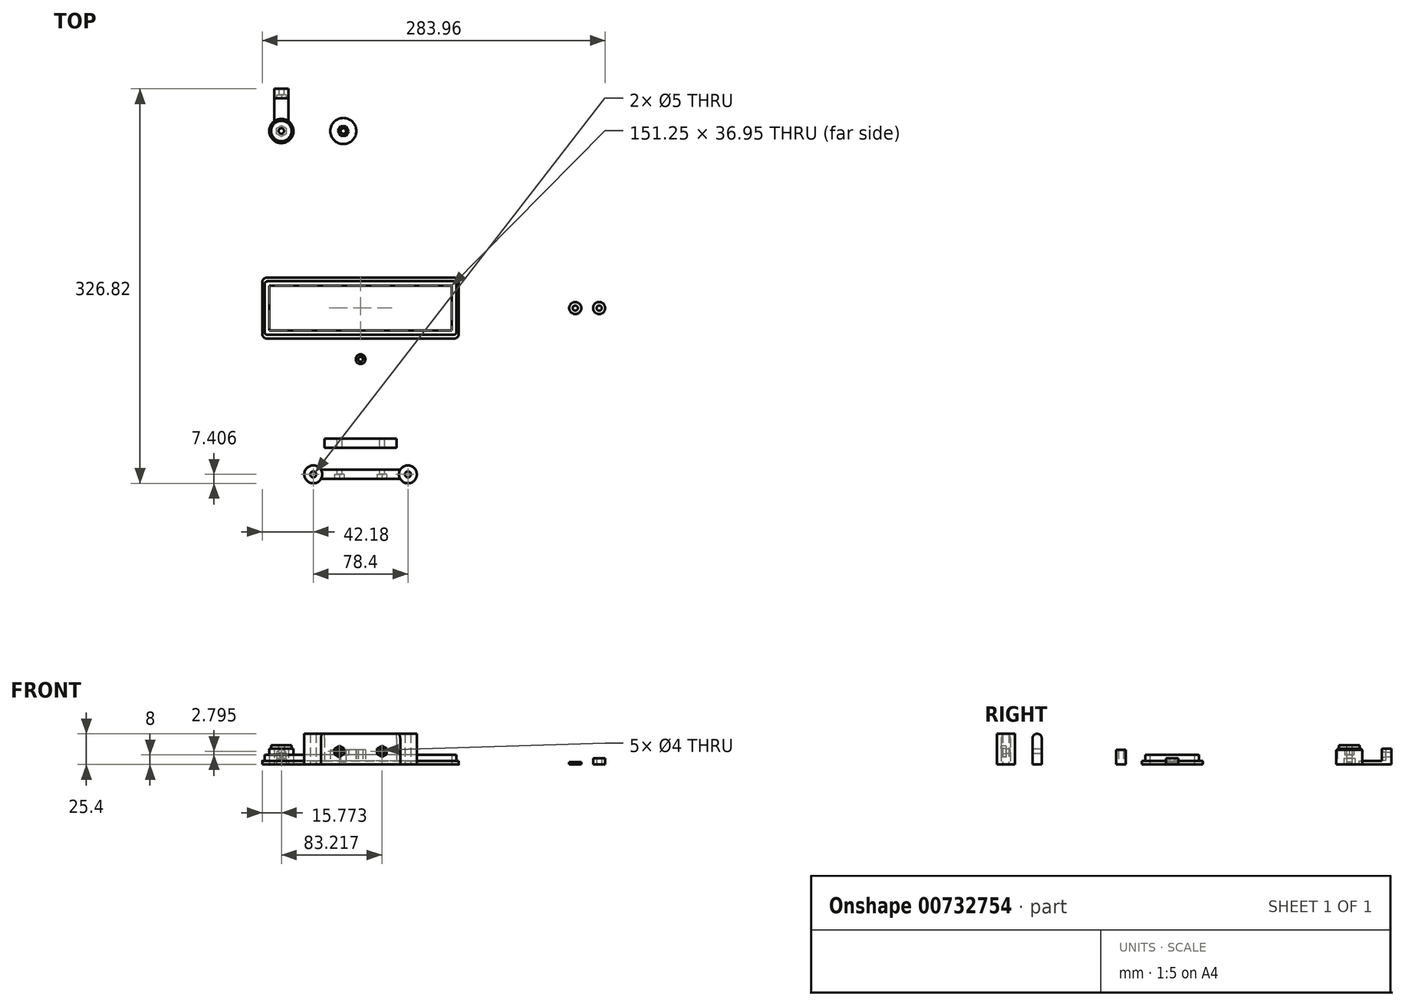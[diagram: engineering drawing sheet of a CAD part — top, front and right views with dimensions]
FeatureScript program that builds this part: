
annotation { "Feature Type Name" : "Feature", "Feature Type Description" : "" }
export const myFeature = defineFeature(function(context is Context, id is Id, definition is map)
    precondition{}
    {
        {
            var Q0;
            Q0=qCreatedBy(makeId("Top.planeOp"),FACE);
            var sketch = newSketch(context, id + "F0", { "sketchPlane" : qUnion([Q0])});
            skLineSegment(sketch, "E0.bottom", {"start": v(79.38, -22.22) * mm, "end": v(-79.38, -22.23) * mm});
            skLineSegment(sketch, "E0.top", {"start": v(79.38, 22.23) * mm, "end": v(-79.38, 22.23) * mm});
            skLineSegment(sketch, "E0.left", {"start": v(79.38, -22.22) * mm, "end": v(79.38, 22.23) * mm});
            skLineSegment(sketch, "E0.right", {"start": v(-79.38, -22.23) * mm, "end": v(-79.38, 22.22) * mm});
            skPoint(sketch, "E0.middle", {"position": v(0, 0) * mm});
            skLineSegment(sketch, "E1.bottom", {"start": v(77.57, -25.22) * mm, "end": v(-77.57, -25.23) * mm});
            skLineSegment(sketch, "E1.top", {"start": v(77.57, 25.23) * mm, "end": v(-77.57, 25.22) * mm});
            skLineSegment(sketch, "E1.left", {"start": v(81.38, -21.41) * mm, "end": v(81.38, 21.42) * mm});
            skLineSegment(sketch, "E1.right", {"start": v(-81.38, -21.42) * mm, "end": v(-81.38, 21.41) * mm});
            skLineSegment(sketch, "E2.bottom", {"start": v(-78.62, 21.47) * mm, "end": v(-68.62, 21.47) * mm});
            skLineSegment(sketch, "E2.top", {"start": v(-78.62, 18.47) * mm, "end": v(-68.62, 18.47) * mm});
            skLineSegment(sketch, "E2.left", {"start": v(-78.62, 21.47) * mm, "end": v(-78.62, 18.47) * mm});
            skLineSegment(sketch, "E2.right", {"start": v(-68.62, 21.47) * mm, "end": v(-68.62, 18.47) * mm});
            skLineSegment(sketch, "E3.bottom", {"start": v(-78.62, 21.47) * mm, "end": v(-75.62, 21.47) * mm});
            skLineSegment(sketch, "E3.top", {"start": v(-78.62, 11.47) * mm, "end": v(-75.62, 11.47) * mm});
            skLineSegment(sketch, "E3.left", {"start": v(-78.62, 21.47) * mm, "end": v(-78.62, 11.47) * mm});
            skLineSegment(sketch, "E3.right", {"start": v(-75.62, 21.47) * mm, "end": v(-75.62, 11.47) * mm});
            skLineSegment(sketch, "E4.bottom", {"start": v(-78.62, -21.47) * mm, "end": v(-78.62, -11.47) * mm});
            skLineSegment(sketch, "E4.top", {"start": v(-75.62, -21.47) * mm, "end": v(-75.62, -11.47) * mm});
            skLineSegment(sketch, "E4.left", {"start": v(-78.62, -21.47) * mm, "end": v(-75.62, -21.47) * mm});
            skLineSegment(sketch, "E4.right", {"start": v(-78.62, -11.47) * mm, "end": v(-75.62, -11.47) * mm});
            skLineSegment(sketch, "E5.bottom", {"start": v(-78.62, -21.47) * mm, "end": v(-78.62, -18.47) * mm});
            skLineSegment(sketch, "E5.top", {"start": v(-68.62, -21.47) * mm, "end": v(-68.62, -18.47) * mm});
            skLineSegment(sketch, "E5.left", {"start": v(-78.62, -21.47) * mm, "end": v(-68.62, -21.47) * mm});
            skLineSegment(sketch, "E5.right", {"start": v(-78.62, -18.47) * mm, "end": v(-68.62, -18.47) * mm});
            skLineSegment(sketch, "E6.bottom", {"start": v(78.62, -21.48) * mm, "end": v(68.62, -21.48) * mm});
            skLineSegment(sketch, "E6.top", {"start": v(78.62, -18.48) * mm, "end": v(68.62, -18.48) * mm});
            skLineSegment(sketch, "E6.left", {"start": v(78.62, -21.48) * mm, "end": v(78.62, -18.48) * mm});
            skLineSegment(sketch, "E6.right", {"start": v(68.62, -21.48) * mm, "end": v(68.62, -18.48) * mm});
            skLineSegment(sketch, "E7.bottom", {"start": v(78.62, -21.48) * mm, "end": v(75.62, -21.48) * mm});
            skLineSegment(sketch, "E7.top", {"start": v(78.62, -11.48) * mm, "end": v(75.62, -11.48) * mm});
            skLineSegment(sketch, "E7.left", {"start": v(78.62, -21.48) * mm, "end": v(78.62, -11.48) * mm});
            skLineSegment(sketch, "E7.right", {"start": v(75.62, -21.48) * mm, "end": v(75.62, -11.48) * mm});
            skLineSegment(sketch, "E8.bottom", {"start": v(78.62, 21.48) * mm, "end": v(78.62, 11.48) * mm});
            skLineSegment(sketch, "E8.top", {"start": v(75.62, 21.48) * mm, "end": v(75.62, 11.48) * mm});
            skLineSegment(sketch, "E8.left", {"start": v(78.62, 21.48) * mm, "end": v(75.62, 21.48) * mm});
            skLineSegment(sketch, "E8.right", {"start": v(78.62, 11.48) * mm, "end": v(75.62, 11.48) * mm});
            skLineSegment(sketch, "E9.bottom", {"start": v(78.62, 21.48) * mm, "end": v(78.62, 18.48) * mm});
            skLineSegment(sketch, "E9.top", {"start": v(68.62, 21.48) * mm, "end": v(68.62, 18.48) * mm});
            skLineSegment(sketch, "E9.left", {"start": v(78.62, 21.48) * mm, "end": v(68.62, 21.48) * mm});
            skLineSegment(sketch, "E9.right", {"start": v(78.62, 18.48) * mm, "end": v(68.62, 18.48) * mm});
            skPoint(sketch, "E10.visualSharp", {"position": v(-81.38, 25.22) * mm});
            skArc(sketch, "E10.filletArc", {"start": v(-77.57, 25.22) * mm, "mid": v(-80.26, 24.1) * mm, "end": v(-81.38, 21.41) * mm});
            skPoint(sketch, "E11.visualSharp", {"position": v(-81.38, -25.23) * mm});
            skArc(sketch, "E11.filletArc", {"start": v(-81.37, -21.42) * mm, "mid": v(-80.26, -24.1) * mm, "end": v(-77.57, -25.22) * mm});
            skPoint(sketch, "E12.visualSharp", {"position": v(81.38, 25.23) * mm});
            skArc(sketch, "E12.filletArc", {"start": v(81.37, 21.42) * mm, "mid": v(80.26, 24.1) * mm, "end": v(77.57, 25.22) * mm});
            skPoint(sketch, "E13.visualSharp", {"position": v(81.38, -25.22) * mm});
            skArc(sketch, "E13.filletArc", {"start": v(77.57, -25.22) * mm, "mid": v(80.26, -24.1) * mm, "end": v(81.37, -21.41) * mm});
            skLineSegment(sketch, "E14", {"start": v(-75.62, 11.47) * mm, "end": v(-75.62, -11.47) * mm});
            skLineSegment(sketch, "E15", {"start": v(-68.63, 18.47) * mm, "end": v(68.62, 18.48) * mm});
            skLineSegment(sketch, "E16", {"start": v(75.62, 11.48) * mm, "end": v(75.62, -11.48) * mm});
            skLineSegment(sketch, "E17", {"start": v(68.62, -18.48) * mm, "end": v(-68.63, -18.47) * mm});
            skLineSegment(sketch, "E18.bottom", {"start": v(-58.1, 25.22) * mm, "end": v(-38.1, 25.22) * mm});
            skLineSegment(sketch, "E18.top", {"start": v(-58.1, 40.23) * mm, "end": v(-38.1, 40.23) * mm});
            skLineSegment(sketch, "E18.left", {"start": v(-58.1, 25.23) * mm, "end": v(-58.1, 40.23) * mm});
            skLineSegment(sketch, "E18.right", {"start": v(-38.1, 25.23) * mm, "end": v(-38.1, 40.23) * mm});
            skLineSegment(sketch, "E19.bottom", {"start": v(58.1, 25.23) * mm, "end": v(38.1, 25.23) * mm});
            skLineSegment(sketch, "E19.top", {"start": v(58.1, 40.23) * mm, "end": v(38.1, 40.23) * mm});
            skLineSegment(sketch, "E19.left", {"start": v(58.1, 25.22) * mm, "end": v(58.1, 40.23) * mm});
            skLineSegment(sketch, "E19.right", {"start": v(38.1, 25.22) * mm, "end": v(38.1, 40.23) * mm});
            skCircle(sketch, "E20", {"center": v(-48.1, 32.73) * mm, "radius": 2.25 * mm});
            skCircle(sketch, "E21", {"center": v(48.1, 32.73) * mm, "radius": 2.25 * mm});
            skLineSegment(sketch, "E22", {"start": v(-68.63, 21.47) * mm, "end": v(68.62, 21.48) * mm});
            skLineSegment(sketch, "E23", {"start": v(68.62, 18.48) * mm, "end": v(-68.63, 18.47) * mm});
            skLineSegment(sketch, "E24", {"start": v(-78.62, -11.47) * mm, "end": v(-78.62, 11.47) * mm});
            skLineSegment(sketch, "E25", {"start": v(-68.63, -18.48) * mm, "end": v(68.62, -18.48) * mm});
            skLineSegment(sketch, "E26", {"start": v(68.62, -21.48) * mm, "end": v(-68.63, -21.47) * mm});
            skSolve(sketch);
        }
        {
            var Q0;
            Q0=makeQuery(id+"F0.imprint","IMPRINT",FACE,{"disambiguationData":[TD([[makeQuery(id+"F0.imprint","IMPRINT",EDGE,{"derivedFrom":sQuery(id+"F0.wireOp",EDGE,"E0.bottom")}),1.0]])]});
            var Q1;
            Q1=makeQuery(id+"F0.imprint","IMPRINT",FACE,{"disambiguationData":[TD([[makeQuery(id+"F0.imprint","IMPRINT",EDGE,{"derivedFrom":sQuery(id+"F0.wireOp",EDGE,"E0.bottom")}),-1.0]])]});
            var Q2;
            {var subQ0=sQuery(id+"F0.wireOp",EDGE,"E2.bottom");Q2=makeQuery(id+"F0.imprint","IMPRINT",FACE,{"disambiguationData":[TD([[makeQuery(id+"F0.imprint","IMPRINT",EDGE,{"derivedFrom":subQ0}),-1.0]])]});}
            var Q3;
            {var subQ5=sQuery(id+"F0.wireOp",EDGE,"E3.bottom");Q3=makeQuery(id+"F0.imprint","IMPRINT",FACE,{"disambiguationData":[TD([[makeQuery(id+"F0.imprint","IMPRINT",EDGE,{"derivedFrom":subQ5}),-1.0]])]});}
            var Q4;
            {var subQ5=sQuery(id+"F0.wireOp",EDGE,"E3.top");Q4=makeQuery(id+"F0.imprint","IMPRINT",FACE,{"disambiguationData":[TD([[makeQuery(id+"F0.imprint","IMPRINT",EDGE,{"derivedFrom":subQ5}),1.0]])]});}
            var Q5;
            {var subQ0=sQuery(id+"F0.wireOp",EDGE,"E4.bottom");Q5=makeQuery(id+"F0.imprint","IMPRINT",FACE,{"disambiguationData":[TD([[makeQuery(id+"F0.imprint","IMPRINT",EDGE,{"derivedFrom":subQ0}),-1.0]])]});}
            var Q6;
            {var subQ5=sQuery(id+"F0.wireOp",EDGE,"E5.bottom");Q6=makeQuery(id+"F0.imprint","IMPRINT",FACE,{"disambiguationData":[TD([[makeQuery(id+"F0.imprint","IMPRINT",EDGE,{"derivedFrom":subQ5}),-1.0]])]});}
            var Q7;
            {var subQ5=sQuery(id+"F0.wireOp",EDGE,"E5.top");Q7=makeQuery(id+"F0.imprint","IMPRINT",FACE,{"disambiguationData":[TD([[makeQuery(id+"F0.imprint","IMPRINT",EDGE,{"derivedFrom":subQ5}),1.0]])]});}
            var Q8;
            {var subQ5=sQuery(id+"F0.wireOp",EDGE,"E9.top");Q8=makeQuery(id+"F0.imprint","IMPRINT",FACE,{"disambiguationData":[TD([[makeQuery(id+"F0.imprint","IMPRINT",EDGE,{"derivedFrom":subQ5}),1.0]])]});}
            var Q9;
            {var subQ5=sQuery(id+"F0.wireOp",EDGE,"E9.bottom");Q9=makeQuery(id+"F0.imprint","IMPRINT",FACE,{"disambiguationData":[TD([[makeQuery(id+"F0.imprint","IMPRINT",EDGE,{"derivedFrom":subQ5}),-1.0]])]});}
            var Q10;
            {var subQ0=sQuery(id+"F0.wireOp",EDGE,"E8.bottom");Q10=makeQuery(id+"F0.imprint","IMPRINT",FACE,{"disambiguationData":[TD([[makeQuery(id+"F0.imprint","IMPRINT",EDGE,{"derivedFrom":subQ0}),-1.0]])]});}
            var Q11;
            {var subQ5=sQuery(id+"F0.wireOp",EDGE,"E7.top");Q11=makeQuery(id+"F0.imprint","IMPRINT",FACE,{"disambiguationData":[TD([[makeQuery(id+"F0.imprint","IMPRINT",EDGE,{"derivedFrom":subQ5}),1.0]])]});}
            var Q12;
            {var subQ0=sQuery(id+"F0.wireOp",EDGE,"E6.bottom");Q12=makeQuery(id+"F0.imprint","IMPRINT",FACE,{"disambiguationData":[TD([[makeQuery(id+"F0.imprint","IMPRINT",EDGE,{"derivedFrom":subQ0}),-1.0]])]});}
            var Q13;
            {var subQ5=sQuery(id+"F0.wireOp",EDGE,"E7.bottom");Q13=makeQuery(id+"F0.imprint","IMPRINT",FACE,{"disambiguationData":[TD([[makeQuery(id+"F0.imprint","IMPRINT",EDGE,{"derivedFrom":subQ5}),-1.0]])]});}
            var Q14;
            Q14=makeQuery(id+"F0.imprint","IMPRINT",FACE,{"disambiguationData":[TD([[makeQuery(id+"F0.imprint","IMPRINT",EDGE,{"derivedFrom":sQuery(id+"F0.wireOp",EDGE,"E18.bottom")}),1.0]])]});
            var Q15;
            Q15=makeQuery(id+"F0.imprint","IMPRINT",FACE,{"disambiguationData":[TD([[makeQuery(id+"F0.imprint","IMPRINT",EDGE,{"derivedFrom":sQuery(id+"F0.wireOp",EDGE,"E19.bottom")}),-1.0]])]});
            var Q16;
            Q16=makeQuery(id+"F0.imprint","IMPRINT",FACE,{"disambiguationData":[TD([[makeQuery(id+"F0.imprint","IMPRINT",EDGE,{"derivedFrom":sQuery(id+"F0.wireOp",EDGE,"E2.right")}),1.0]])]});
            var Q17;
            Q17=makeQuery(id+"F0.imprint","IMPRINT",FACE,{"disambiguationData":[TD([[makeQuery(id+"F0.imprint","IMPRINT",EDGE,{"derivedFrom":sQuery(id+"F0.wireOp",EDGE,"E3.top")}),-1.0]])]});
            var Q18;
            Q18=makeQuery(id+"F0.imprint","IMPRINT",FACE,{"disambiguationData":[TD([[makeQuery(id+"F0.imprint","IMPRINT",EDGE,{"derivedFrom":sQuery(id+"F0.wireOp",EDGE,"E5.top")}),-1.0]])]});
            extrude(context, id + "F1", {"entities" : qUnion([Q0, Q1, Q2, Q3, Q4, Q5, Q6, Q7, Q8, Q9, Q10, Q11, Q12, Q13, Q14, Q15, Q16, Q17, Q18]), "depth" : 3 * mm, "offsetDistance" : 25.4 * mm});
        }
        {
            var Q0;
            {var subQ5=sQuery(id+"F0.wireOp",EDGE,"E9.top");Q0=makeQuery(id+"F0.imprint","IMPRINT",FACE,{"disambiguationData":[TD([[makeQuery(id+"F0.imprint","IMPRINT",EDGE,{"derivedFrom":subQ5}),1.0]])]});}
            var Q1;
            {var subQ5=sQuery(id+"F0.wireOp",EDGE,"E9.bottom");Q1=makeQuery(id+"F0.imprint","IMPRINT",FACE,{"disambiguationData":[TD([[makeQuery(id+"F0.imprint","IMPRINT",EDGE,{"derivedFrom":subQ5}),-1.0]])]});}
            var Q2;
            {var subQ0=sQuery(id+"F0.wireOp",EDGE,"E8.bottom");Q2=makeQuery(id+"F0.imprint","IMPRINT",FACE,{"disambiguationData":[TD([[makeQuery(id+"F0.imprint","IMPRINT",EDGE,{"derivedFrom":subQ0}),-1.0]])]});}
            var Q3;
            Q3=makeQuery(id+"F0.imprint","IMPRINT",FACE,{"disambiguationData":[TD([[makeQuery(id+"F0.imprint","IMPRINT",EDGE,{"derivedFrom":sQuery(id+"F0.wireOp",EDGE,"E2.right")}),1.0]])]});
            var Q4;
            Q4=makeQuery(id+"F0.imprint","IMPRINT",FACE,{"disambiguationData":[TD([[makeQuery(id+"F0.imprint","IMPRINT",EDGE,{"derivedFrom":sQuery(id+"F0.wireOp",EDGE,"E0.bottom")}),-1.0]])]});
            var Q5;
            {var subQ5=sQuery(id+"F0.wireOp",EDGE,"E7.top");Q5=makeQuery(id+"F0.imprint","IMPRINT",FACE,{"disambiguationData":[TD([[makeQuery(id+"F0.imprint","IMPRINT",EDGE,{"derivedFrom":subQ5}),1.0]])]});}
            var Q6;
            {var subQ5=sQuery(id+"F0.wireOp",EDGE,"E7.bottom");Q6=makeQuery(id+"F0.imprint","IMPRINT",FACE,{"disambiguationData":[TD([[makeQuery(id+"F0.imprint","IMPRINT",EDGE,{"derivedFrom":subQ5}),-1.0]])]});}
            var Q7;
            {var subQ0=sQuery(id+"F0.wireOp",EDGE,"E6.bottom");Q7=makeQuery(id+"F0.imprint","IMPRINT",FACE,{"disambiguationData":[TD([[makeQuery(id+"F0.imprint","IMPRINT",EDGE,{"derivedFrom":subQ0}),-1.0]])]});}
            var Q8;
            Q8=makeQuery(id+"F0.imprint","IMPRINT",FACE,{"disambiguationData":[TD([[makeQuery(id+"F0.imprint","IMPRINT",EDGE,{"derivedFrom":sQuery(id+"F0.wireOp",EDGE,"E5.top")}),-1.0]])]});
            var Q9;
            {var subQ0=sQuery(id+"F0.wireOp",EDGE,"E2.bottom");Q9=makeQuery(id+"F0.imprint","IMPRINT",FACE,{"disambiguationData":[TD([[makeQuery(id+"F0.imprint","IMPRINT",EDGE,{"derivedFrom":subQ0}),-1.0]])]});}
            var Q10;
            {var subQ5=sQuery(id+"F0.wireOp",EDGE,"E3.bottom");Q10=makeQuery(id+"F0.imprint","IMPRINT",FACE,{"disambiguationData":[TD([[makeQuery(id+"F0.imprint","IMPRINT",EDGE,{"derivedFrom":subQ5}),-1.0]])]});}
            var Q11;
            {var subQ5=sQuery(id+"F0.wireOp",EDGE,"E3.top");Q11=makeQuery(id+"F0.imprint","IMPRINT",FACE,{"disambiguationData":[TD([[makeQuery(id+"F0.imprint","IMPRINT",EDGE,{"derivedFrom":subQ5}),1.0]])]});}
            var Q12;
            Q12=makeQuery(id+"F0.imprint","IMPRINT",FACE,{"disambiguationData":[TD([[makeQuery(id+"F0.imprint","IMPRINT",EDGE,{"derivedFrom":sQuery(id+"F0.wireOp",EDGE,"E3.top")}),-1.0]])]});
            var Q13;
            {var subQ0=sQuery(id+"F0.wireOp",EDGE,"E4.bottom");Q13=makeQuery(id+"F0.imprint","IMPRINT",FACE,{"disambiguationData":[TD([[makeQuery(id+"F0.imprint","IMPRINT",EDGE,{"derivedFrom":subQ0}),-1.0]])]});}
            var Q14;
            {var subQ5=sQuery(id+"F0.wireOp",EDGE,"E5.bottom");Q14=makeQuery(id+"F0.imprint","IMPRINT",FACE,{"disambiguationData":[TD([[makeQuery(id+"F0.imprint","IMPRINT",EDGE,{"derivedFrom":subQ5}),-1.0]])]});}
            var Q15;
            {var subQ5=sQuery(id+"F0.wireOp",EDGE,"E5.top");Q15=makeQuery(id+"F0.imprint","IMPRINT",FACE,{"disambiguationData":[TD([[makeQuery(id+"F0.imprint","IMPRINT",EDGE,{"derivedFrom":subQ5}),1.0]])]});}
            extrude(context, id + "F2", {"entities" : qUnion([Q0, Q1, Q2, Q3, Q4, Q5, Q6, Q7, Q8, Q9, Q10, Q11, Q12, Q13, Q14, Q15]), "operationType" : NewBodyOperationType.ADD, "depth" : 8 * mm, "offsetDistance" : 25.4 * mm});
        }
        {
            var Q0;
            Q0=makeQuery(id+"F2.opExtrude","SWEPT_EDGE",EDGE,{"disambiguationData":[OSD([sQuery(id+"F0.wireOp",EDGE,"E3.bottom"),sQuery(id+"F0.wireOp",EDGE,"E3.left")])]});
            var Q1;
            Q1=makeQuery(id+"F2.opExtrude","SWEPT_EDGE",EDGE,{"disambiguationData":[OSD([sQuery(id+"F0.wireOp",EDGE,"E5.bottom"),sQuery(id+"F0.wireOp",EDGE,"E5.left")])]});
            var Q2;
            Q2=makeQuery(id+"F2.opExtrude","SWEPT_EDGE",EDGE,{"disambiguationData":[OSD([sQuery(id+"F0.wireOp",EDGE,"E9.bottom"),sQuery(id+"F0.wireOp",EDGE,"E9.left")])]});
            var Q3;
            Q3=makeQuery(id+"F2.opExtrude","SWEPT_EDGE",EDGE,{"disambiguationData":[OSD([sQuery(id+"F0.wireOp",EDGE,"E7.bottom"),sQuery(id+"F0.wireOp",EDGE,"E7.left")])]});
            var Q4;
            Q4=makeQuery(id+"F1.opExtrude","SWEPT_EDGE",EDGE,{"disambiguationData":[OSD([sQuery(id+"F0.wireOp",EDGE,"E19.top"),sQuery(id+"F0.wireOp",EDGE,"E19.left")])]});
            var Q5;
            Q5=makeQuery(id+"F1.opExtrude","SWEPT_EDGE",EDGE,{"disambiguationData":[OSD([sQuery(id+"F0.wireOp",EDGE,"E19.top"),sQuery(id+"F0.wireOp",EDGE,"E19.right")])]});
            var Q6;
            Q6=makeQuery(id+"F1.opExtrude","SWEPT_EDGE",EDGE,{"disambiguationData":[OSD([sQuery(id+"F0.wireOp",EDGE,"E18.top"),sQuery(id+"F0.wireOp",EDGE,"E18.right")])]});
            var Q7;
            Q7=makeQuery(id+"F1.opExtrude","SWEPT_EDGE",EDGE,{"disambiguationData":[OSD([sQuery(id+"F0.wireOp",EDGE,"E18.top"),sQuery(id+"F0.wireOp",EDGE,"E18.left")])]});
            var Q8;
            Q8=makeQuery(id+"F2.opExtrude","SWEPT_EDGE",EDGE,{"disambiguationData":[OSD([sQuery(id+"F0.wireOp",EDGE,"E0.top"),sQuery(id+"F0.wireOp",EDGE,"E0.right")])]});
            var Q9;
            Q9=makeQuery(id+"F2.opExtrude","SWEPT_EDGE",EDGE,{"disambiguationData":[OSD([sQuery(id+"F0.wireOp",EDGE,"E0.bottom"),sQuery(id+"F0.wireOp",EDGE,"E0.right")])]});
            var Q10;
            Q10=makeQuery(id+"F2.opExtrude","SWEPT_EDGE",EDGE,{"disambiguationData":[OSD([sQuery(id+"F0.wireOp",EDGE,"E0.top"),sQuery(id+"F0.wireOp",EDGE,"E0.left")])]});
            var Q11;
            Q11=makeQuery(id+"F2.opExtrude","SWEPT_EDGE",EDGE,{"disambiguationData":[OSD([sQuery(id+"F0.wireOp",EDGE,"E0.bottom"),sQuery(id+"F0.wireOp",EDGE,"E0.left")])]});
            fillet(context, id + "F3", {"entities" : qUnion([Q0, Q1, Q2, Q3, Q4, Q5, Q6, Q7, Q8, Q9, Q10, Q11]), "radius" : 2.54 * mm, "tangentPropagation" : true, "allowEdgeOverflow" : false});
        }
        {
            var Q0;
            Q0=qCreatedBy(makeId("Top.planeOp"),FACE);
            var sketch = newSketch(context, id + "F4", { "sketchPlane" : qUnion([Q0])});
            skCircle(sketch, "E27", {"center": v(-65.6, 146.68) * mm, "radius": 10 * mm});
            skCircle(sketch, "E28", {"center": v(-65.6, 146.68) * mm, "radius": 2.25 * mm});
            skCircle(sketch, "E29", {"center": v(-65.6, 146.68) * mm, "radius": 8.5 * mm});
            skLineSegment(sketch, "E30.bottom", {"start": v(-71.6, 146.68) * mm, "end": v(-59.6, 146.68) * mm});
            skLineSegment(sketch, "E30.top", {"start": v(-71.6, 181.68) * mm, "end": v(-59.6, 181.68) * mm});
            skLineSegment(sketch, "E30.left", {"start": v(-71.6, 146.68) * mm, "end": v(-71.6, 181.68) * mm});
            skLineSegment(sketch, "E30.right", {"start": v(-59.6, 146.68) * mm, "end": v(-59.6, 181.68) * mm});
            skLineSegment(sketch, "E31.top", {"start": v(-71.6, 173.68) * mm, "end": v(-59.6, 173.68) * mm});
            skLineSegment(sketch, "E31.left", {"start": v(-71.6, 181.68) * mm, "end": v(-71.6, 173.68) * mm});
            skLineSegment(sketch, "E31.right", {"start": v(-59.6, 181.68) * mm, "end": v(-59.6, 173.68) * mm});
            skCircle(sketch, "E32.cCircle", {"center": v(-65.6, 146.68) * mm, "radius": 4 * mm, "construction": true});
            skLineSegment(sketch, "E32.0", {"start": v(-65.6, 151.3) * mm, "end": v(-61.6, 149) * mm});
            skLineSegment(sketch, "E32.1", {"start": v(-61.6, 149) * mm, "end": v(-61.6, 144.38) * mm});
            skLineSegment(sketch, "E32.2", {"start": v(-61.6, 144.38) * mm, "end": v(-65.6, 142.07) * mm});
            skLineSegment(sketch, "E32.3", {"start": v(-65.6, 142.07) * mm, "end": v(-69.6, 144.38) * mm});
            skLineSegment(sketch, "E32.4", {"start": v(-69.6, 144.38) * mm, "end": v(-69.6, 149) * mm});
            skLineSegment(sketch, "E32.5", {"start": v(-69.6, 149) * mm, "end": v(-65.6, 151.3) * mm});
            skPoint(sketch, "E32.0.midPoint", {"position": v(-63.6, 150.15) * mm});
            skSolve(sketch);
        }
        {
            var Q0;
            {var subQ13=sQuery(id+"F4.wireOp",EDGE,"E32.2");Q0=makeQuery(id+"F4.imprint","IMPRINT",FACE,{"disambiguationData":[TD([[makeQuery(id+"F4.imprint","IMPRINT",EDGE,{"derivedFrom":subQ13}),1.0]])]});}
            var Q1;
            {var subQ0=sQuery(id+"F4.wireOp",EDGE,"E30.left");var subQ1=sQuery(id+"F4.wireOp",EDGE,"E27");var subQ2=makeQuery(id+"F4.imprint","INTERSECT",VERTEX,{"derivedFrom":[subQ1,subQ0]});Q1=makeQuery(id+"F4.imprint","IMPRINT",FACE,{"disambiguationData":[TD([[makeQuery(id+"F4.imprint","IMPRINT",EDGE,{"disambiguationData":[TD([[subQ2,-1.0]])],"derivedFrom":subQ1}),1.0]])]});}
            var Q2;
            {var subQ5=sQuery(id+"F4.wireOp",EDGE,"E32.0");Q2=makeQuery(id+"F4.imprint","IMPRINT",FACE,{"disambiguationData":[TD([[makeQuery(id+"F4.imprint","IMPRINT",EDGE,{"derivedFrom":subQ5}),1.0]])]});}
            var Q3;
            {var subQ0=sQuery(id+"F4.wireOp",EDGE,"E30.left");var subQ1=sQuery(id+"F4.wireOp",EDGE,"E27");var subQ2=makeQuery(id+"F4.imprint","INTERSECT",VERTEX,{"derivedFrom":[subQ1,subQ0]});Q3=makeQuery(id+"F4.imprint","IMPRINT",FACE,{"disambiguationData":[TD([[makeQuery(id+"F4.imprint","IMPRINT",EDGE,{"disambiguationData":[TD([[subQ2,1.0]])],"derivedFrom":subQ1}),1.0]])]});}
            var Q4;
            {var subQ0=sQuery(id+"F4.wireOp",EDGE,"E32.0");Q4=makeQuery(id+"F4.imprint","IMPRINT",FACE,{"disambiguationData":[TD([[makeQuery(id+"F4.imprint","IMPRINT",EDGE,{"derivedFrom":subQ0}),-1.0]])]});}
            var Q5;
            {var subQ8=sQuery(id+"F4.wireOp",EDGE,"E32.2");Q5=makeQuery(id+"F4.imprint","IMPRINT",FACE,{"disambiguationData":[TD([[makeQuery(id+"F4.imprint","IMPRINT",EDGE,{"derivedFrom":subQ8}),-1.0]])]});}
            extrude(context, id + "F5", {"entities" : qUnion([Q0, Q1, Q2, Q3, Q4, Q5]), "depth" : 13 * mm, "offsetDistance" : 25.4 * mm});
        }
        {
            var Q0;
            {var subQ8=sQuery(id+"F4.wireOp",EDGE,"E32.2");Q0=makeQuery(id+"F4.imprint","IMPRINT",FACE,{"disambiguationData":[TD([[makeQuery(id+"F4.imprint","IMPRINT",EDGE,{"derivedFrom":subQ8}),-1.0]])]});}
            var Q1;
            {var subQ0=sQuery(id+"F4.wireOp",EDGE,"E32.0");Q1=makeQuery(id+"F4.imprint","IMPRINT",FACE,{"disambiguationData":[TD([[makeQuery(id+"F4.imprint","IMPRINT",EDGE,{"derivedFrom":subQ0}),-1.0]])]});}
            extrude(context, id + "F6", {"entities" : qUnion([Q0, Q1]), "operationType" : NewBodyOperationType.REMOVE, "depth" : 9 * mm, "offsetDistance" : 25.4 * mm});
        }
        {
            var Q0;
            {var subQ0=sQuery(id+"F4.wireOp",EDGE,"E30.left");var subQ1=sQuery(id+"F4.wireOp",EDGE,"E27");var subQ2=makeQuery(id+"F4.imprint","INTERSECT",VERTEX,{"derivedFrom":[subQ1,subQ0]});Q0=makeQuery(id+"F4.imprint","IMPRINT",FACE,{"disambiguationData":[TD([[makeQuery(id+"F4.imprint","IMPRINT",EDGE,{"disambiguationData":[TD([[subQ2,1.0]])],"derivedFrom":subQ1}),1.0]])]});}
            var Q1;
            {var subQ5=sQuery(id+"F4.wireOp",EDGE,"E31.top");Q1=makeQuery(id+"F4.imprint","IMPRINT",FACE,{"disambiguationData":[TD([[makeQuery(id+"F4.imprint","IMPRINT",EDGE,{"derivedFrom":subQ5}),-1.0]])]});}
            var Q2;
            Q2=makeQuery(id+"F4.imprint","IMPRINT",FACE,{"disambiguationData":[TD([[makeQuery(id+"F4.imprint","IMPRINT",EDGE,{"derivedFrom":sQuery(id+"F4.wireOp",EDGE,"E30.top")}),-1.0]])]});
            extrude(context, id + "F7", {"entities" : qUnion([Q0, Q1, Q2]), "operationType" : NewBodyOperationType.ADD, "depth" : 3 * mm, "offsetDistance" : 25.4 * mm});
        }
        {
            var Q0;
            {var subQ13=sQuery(id+"F4.wireOp",EDGE,"E32.2");Q0=makeQuery(id+"F4.imprint","IMPRINT",FACE,{"disambiguationData":[TD([[makeQuery(id+"F4.imprint","IMPRINT",EDGE,{"derivedFrom":subQ13}),1.0]])]});}
            var Q1;
            {var subQ5=sQuery(id+"F4.wireOp",EDGE,"E32.0");Q1=makeQuery(id+"F4.imprint","IMPRINT",FACE,{"disambiguationData":[TD([[makeQuery(id+"F4.imprint","IMPRINT",EDGE,{"derivedFrom":subQ5}),1.0]])]});}
            var Q2;
            {var subQ0=sQuery(id+"F4.wireOp",EDGE,"E32.0");Q2=makeQuery(id+"F4.imprint","IMPRINT",FACE,{"disambiguationData":[TD([[makeQuery(id+"F4.imprint","IMPRINT",EDGE,{"derivedFrom":subQ0}),-1.0]])]});}
            var Q3;
            {var subQ8=sQuery(id+"F4.wireOp",EDGE,"E32.2");Q3=makeQuery(id+"F4.imprint","IMPRINT",FACE,{"disambiguationData":[TD([[makeQuery(id+"F4.imprint","IMPRINT",EDGE,{"derivedFrom":subQ8}),-1.0]])]});}
            extrude(context, id + "F8", {"entities" : qUnion([Q0, Q1, Q2, Q3]), "operationType" : NewBodyOperationType.ADD, "depth" : 16 * mm, "offsetDistance" : 25.4 * mm, "hasSecondDirection" : true, "secondDirectionOppositeDirection" : false, "secondDirectionDepth" : 5 * mm});
        }
        {
            var Q0;
            Q0=makeQuery(id+"F4.imprint","IMPRINT",FACE,{"disambiguationData":[TD([[makeQuery(id+"F4.imprint","IMPRINT",EDGE,{"derivedFrom":sQuery(id+"F4.wireOp",EDGE,"E30.top")}),-1.0]])]});
            extrude(context, id + "F9", {"entities" : qUnion([Q0]), "operationType" : NewBodyOperationType.ADD, "depth" : 13 * mm, "offsetDistance" : 25.4 * mm});
        }
        {
            var Q0;
            Q0=makeQuery(id+"F9.opExtrude","SWEPT_FACE",FACE,{"disambiguationData":[OSD([sQuery(id+"F4.wireOp",EDGE,"E31.top")])]});
            var sketch = newSketch(context, id + "F10", { "sketchPlane" : qUnion([Q0])});
            skLineSegment(sketch, "E33.0", {"start": v(-71.6, 13) * mm, "end": v(-59.6, 13) * mm});
            skLineSegment(sketch, "E33.1", {"start": v(-71.6, 13) * mm, "end": v(-71.6, 3) * mm});
            skLineSegment(sketch, "E33.2", {"start": v(-59.6, 3) * mm, "end": v(-71.6, 3) * mm});
            skLineSegment(sketch, "E33.3", {"start": v(-59.6, 13) * mm, "end": v(-59.6, 3) * mm});
            skCircle(sketch, "E34", {"center": v(-65.6, 8) * mm, "radius": 2 * mm});
            skCircle(sketch, "E35.cCircle", {"center": v(-65.6, 8) * mm, "radius": 4 * mm, "construction": true});
            skLineSegment(sketch, "E35.0", {"start": v(-61.6, 5.7) * mm, "end": v(-65.6, 3.38) * mm});
            skLineSegment(sketch, "E35.1", {"start": v(-65.6, 3.38) * mm, "end": v(-69.6, 5.7) * mm});
            skLineSegment(sketch, "E35.2", {"start": v(-69.6, 5.7) * mm, "end": v(-69.6, 10.3) * mm});
            skLineSegment(sketch, "E35.3", {"start": v(-69.6, 10.3) * mm, "end": v(-65.6, 12.62) * mm});
            skLineSegment(sketch, "E35.4", {"start": v(-65.6, 12.62) * mm, "end": v(-61.6, 10.3) * mm});
            skLineSegment(sketch, "E35.5", {"start": v(-61.6, 10.3) * mm, "end": v(-61.6, 5.7) * mm});
            skPoint(sketch, "E35.0.midPoint", {"position": v(-63.6, 4.54) * mm});
            skSolve(sketch);
        }
        {
            var Q0;
            Q0=makeQuery(id+"F10.imprint","IMPRINT",FACE,{"disambiguationData":[TD([[makeQuery(id+"F10.imprint","IMPRINT",EDGE,{"derivedFrom":sQuery(id+"F10.wireOp",EDGE,"E34")}),1.0]])]});
            extrude(context, id + "F11", {"entities" : qUnion([Q0]), "operationType" : NewBodyOperationType.REMOVE, "oppositeDirection" : true, "depth" : 25.4 * mm, "offsetDistance" : 25.4 * mm});
        }
        {
            var Q0;
            Q0=makeQuery(id+"F10.imprint","IMPRINT",FACE,{"disambiguationData":[TD([[makeQuery(id+"F10.imprint","IMPRINT",EDGE,{"derivedFrom":sQuery(id+"F10.wireOp",EDGE,"E34")}),-1.0]])]});
            extrude(context, id + "F12", {"entities" : qUnion([Q0]), "operationType" : NewBodyOperationType.REMOVE, "oppositeDirection" : true, "depth" : 3 * mm, "offsetDistance" : 25.4 * mm, "hasSecondDirection" : true, "secondDirectionOppositeDirection" : false, "secondDirectionDepth" : 3 * mm});
        }
        {
            var Q0;
            Q0=qCreatedBy(makeId("Top.planeOp"),FACE);
            var sketch = newSketch(context, id + "F13", { "sketchPlane" : qUnion([Q0])});
            skPoint(sketch, "E36.0", {"position": v(-65.6, 146.68) * mm});
            skCircle(sketch, "E36.1", {"center": v(-65.6, 146.68) * mm, "radius": 10 * mm});
            skCircle(sketch, "E37", {"center": v(-14.28, 146.68) * mm, "radius": 10.8 * mm});
            skCircle(sketch, "E38.cCircle", {"center": v(-14.28, 146.68) * mm, "radius": 3.92 * mm, "construction": true});
            skLineSegment(sketch, "E38.0", {"start": v(-9.74, 146.62) * mm, "end": v(-12.06, 142.73) * mm});
            skLineSegment(sketch, "E38.1", {"start": v(-12.06, 142.73) * mm, "end": v(-16.6, 142.8) * mm});
            skLineSegment(sketch, "E38.2", {"start": v(-16.6, 142.8) * mm, "end": v(-18.8, 146.75) * mm});
            skLineSegment(sketch, "E38.3", {"start": v(-18.8, 146.75) * mm, "end": v(-16.49, 150.64) * mm});
            skLineSegment(sketch, "E38.4", {"start": v(-16.49, 150.64) * mm, "end": v(-11.96, 150.58) * mm});
            skLineSegment(sketch, "E38.5", {"start": v(-11.96, 150.58) * mm, "end": v(-9.74, 146.62) * mm});
            skPoint(sketch, "E38.0.midPoint", {"position": v(-10.9, 144.68) * mm});
            skCircle(sketch, "E39", {"center": v(-14.28, 146.68) * mm, "radius": 2.25 * mm});
            skSolve(sketch);
        }
        {
            var Q0;
            Q0=makeQuery(id+"F13.imprint","IMPRINT",FACE,{"disambiguationData":[TD([[makeQuery(id+"F13.imprint","IMPRINT",EDGE,{"derivedFrom":sQuery(id+"F13.wireOp",EDGE,"E38.0")}),1.0]])]});
            var Q1;
            Q1=makeQuery(id+"F13.imprint","IMPRINT",FACE,{"disambiguationData":[TD([[makeQuery(id+"F13.imprint","IMPRINT",EDGE,{"derivedFrom":sQuery(id+"F13.wireOp",EDGE,"E38.0")}),-1.0]])]});
            var Q2;
            Q2=makeQuery(id+"F13.imprint","IMPRINT",FACE,{"disambiguationData":[TD([[makeQuery(id+"F13.imprint","IMPRINT",EDGE,{"derivedFrom":sQuery(id+"F13.wireOp",EDGE,"E39")}),1.0]])]});
            var Q3;
            Q3=makeQuery(id+"F13.imprint","IMPRINT",FACE,{"disambiguationData":[TD([[makeQuery(id+"F13.imprint","IMPRINT",EDGE,{"derivedFrom":sQuery(id+"F13.wireOp",EDGE,"E37")}),1.0]])]});
            extrude(context, id + "F14", {"entities" : qUnion([Q0, Q1, Q2, Q3]), "depth" : 12 * mm, "offsetDistance" : 25.4 * mm});
        }
        {
            var Q0;
            Q0=makeQuery(id+"F13.imprint","IMPRINT",FACE,{"disambiguationData":[TD([[makeQuery(id+"F13.imprint","IMPRINT",EDGE,{"derivedFrom":sQuery(id+"F13.wireOp",EDGE,"E38.0")}),-1.0]])]});
            var Q1;
            Q1=makeQuery(id+"F13.imprint","IMPRINT",FACE,{"disambiguationData":[TD([[makeQuery(id+"F13.imprint","IMPRINT",EDGE,{"derivedFrom":sQuery(id+"F13.wireOp",EDGE,"E39")}),1.0]])]});
            extrude(context, id + "F15", {"entities" : qUnion([Q0, Q1]), "operationType" : NewBodyOperationType.REMOVE, "depth" : 25.4 * mm, "offsetDistance" : 25.4 * mm, "hasSecondDirection" : true, "secondDirectionOppositeDirection" : false, "secondDirectionDepth" : 8 * mm});
        }
        {
            var Q0;
            Q0=makeQuery(id+"F13.imprint","IMPRINT",FACE,{"disambiguationData":[TD([[makeQuery(id+"F13.imprint","IMPRINT",EDGE,{"derivedFrom":sQuery(id+"F13.wireOp",EDGE,"E39")}),1.0]])]});
            extrude(context, id + "F16", {"entities" : qUnion([Q0]), "operationType" : NewBodyOperationType.REMOVE, "depth" : 25.4 * mm, "offsetDistance" : 25.4 * mm, "hasSecondDirection" : true, "secondDirectionOppositeDirection" : false, "secondDirectionDepth" : 2 * mm});
        }
        {
            var Q0;
            Q0=qCreatedBy(makeId("Top.planeOp"),FACE);
            var sketch = newSketch(context, id + "F17", { "sketchPlane" : qUnion([Q0])});
            skCircle(sketch, "E40", {"center": v(0, -42.35) * mm, "radius": 2 * mm});
            skCircle(sketch, "E41", {"center": v(0, -42.35) * mm, "radius": 4 * mm});
            skSolve(sketch);
        }
        {
            var Q0;
            Q0=makeQuery(id+"F17.imprint","IMPRINT",FACE,{"disambiguationData":[TD([[makeQuery(id+"F17.imprint","IMPRINT",EDGE,{"derivedFrom":sQuery(id+"F17.wireOp",EDGE,"E40")}),-1.0]])]});
            extrude(context, id + "F18", {"entities" : qUnion([Q0]), "depth" : 12 * mm, "offsetDistance" : 25.4 * mm});
        }
        {
            var Q0;
            Q0=qCreatedBy(makeId("Top.planeOp"),FACE);
            var sketch = newSketch(context, id + "F19", { "sketchPlane" : qUnion([Q0])});
            skLineSegment(sketch, "E42.bottom", {"start": v(32.85, -141.54) * mm, "end": v(-32.85, -141.54) * mm});
            skLineSegment(sketch, "E42.top", {"start": v(32.85, -133.92) * mm, "end": v(-32.85, -133.92) * mm});
            skLineSegment(sketch, "E42.left", {"start": v(32.85, -141.54) * mm, "end": v(32.85, -133.92) * mm});
            skLineSegment(sketch, "E42.right", {"start": v(-32.85, -141.54) * mm, "end": v(-32.85, -133.92) * mm});
            skPoint(sketch, "E42.middle", {"position": v(0, -137.73) * mm});
            skLineSegment(sketch, "E43", {"start": v(-32.85, -137.73) * mm, "end": v(-39.2, -137.73) * mm});
            skCircle(sketch, "E44", {"center": v(-39.2, -137.73) * mm, "radius": 7.4 * mm});
            skCircle(sketch, "E45", {"center": v(-39.2, -137.73) * mm, "radius": 2.5 * mm});
            skLineSegment(sketch, "E46", {"start": v(32.85, -137.73) * mm, "end": v(39.2, -137.73) * mm});
            skCircle(sketch, "E47", {"center": v(39.2, -137.73) * mm, "radius": 7.4 * mm});
            skCircle(sketch, "E48", {"center": v(39.2, -137.73) * mm, "radius": 2.5 * mm});
            skSolve(sketch);
        }
        {
            var Q0;
            {var subQ0=sQuery(id+"F19.wireOp",EDGE,"E42.bottom");Q0=makeQuery(id+"F19.imprint","IMPRINT",FACE,{"disambiguationData":[TD([[makeQuery(id+"F19.imprint","IMPRINT",EDGE,{"derivedFrom":subQ0}),-1.0]])]});}
            var Q1;
            Q1=makeQuery(id+"F19.imprint","IMPRINT",FACE,{"disambiguationData":[TD([[makeQuery(id+"F19.imprint","IMPRINT",EDGE,{"derivedFrom":sQuery(id+"F19.wireOp",EDGE,"E45")}),-1.0]])]});
            var Q2;
            {var subQ1=sQuery(id+"F19.wireOp",EDGE,"E42.right");var subQ3=makeQuery(id+"F19.imprint","IMPRINT",VERTEX,{"derivedFrom":subQ1});Q2=makeQuery(id+"F19.imprint","IMPRINT",FACE,{"disambiguationData":[TD([[makeQuery(id+"F19.imprint","IMPRINT",EDGE,{"disambiguationData":[TD([[subQ3,1.0]])],"derivedFrom":subQ1}),-1.0]])]});}
            var Q3;
            Q3=makeQuery(id+"F19.imprint","IMPRINT",FACE,{"disambiguationData":[TD([[makeQuery(id+"F19.imprint","IMPRINT",EDGE,{"derivedFrom":sQuery(id+"F19.wireOp",EDGE,"E48")}),-1.0]])]});
            var Q4;
            {var subQ1=sQuery(id+"F19.wireOp",EDGE,"E42.left");var subQ3=makeQuery(id+"F19.imprint","IMPRINT",VERTEX,{"derivedFrom":subQ1});Q4=makeQuery(id+"F19.imprint","IMPRINT",FACE,{"disambiguationData":[TD([[makeQuery(id+"F19.imprint","IMPRINT",EDGE,{"disambiguationData":[TD([[subQ3,1.0]])],"derivedFrom":subQ1}),1.0]])]});}
            extrude(context, id + "F20", {"entities" : qUnion([Q0, Q1, Q2, Q3, Q4]), "depth" : 25.4 * mm, "offsetDistance" : 25.4 * mm});
        }
        {
            var Q0;
            Q0=makeQuery(id+"F20.opExtrude","CAP_EDGE",EDGE,{"disambiguationData":[OSD([sQuery(id+"F19.wireOp",EDGE,"E42.top")])],"isStart":false});
            var Q1;
            Q1=makeQuery(id+"F20.opExtrude","CAP_EDGE",EDGE,{"disambiguationData":[OSD([sQuery(id+"F19.wireOp",EDGE,"E42.bottom")])],"isStart":false});
            fillet(context, id + "F21", {"entities" : qUnion([Q0, Q1]), "radius" : 3.8 * mm, "tangentPropagation" : true, "allowEdgeOverflow" : false});
        }
        {
            var Q0;
            Q0=makeQuery(id+"F20.opExtrude","SWEPT_FACE",FACE,{"disambiguationData":[OSD([sQuery(id+"F19.wireOp",EDGE,"E42.bottom")])]});
            var sketch = newSketch(context, id + "F22", { "sketchPlane" : qUnion([Q0])});
            skCircle(sketch, "E49.cCircle", {"center": v(-17.6, 10.8) * mm, "radius": 4 * mm, "construction": true});
            skLineSegment(sketch, "E49.0", {"start": v(-13.6, 8.49) * mm, "end": v(-17.6, 6.18) * mm});
            skLineSegment(sketch, "E49.1", {"start": v(-17.6, 6.18) * mm, "end": v(-21.6, 8.49) * mm});
            skLineSegment(sketch, "E49.2", {"start": v(-21.6, 8.49) * mm, "end": v(-21.6, 13.1) * mm});
            skLineSegment(sketch, "E49.3", {"start": v(-21.6, 13.1) * mm, "end": v(-17.6, 15.41) * mm});
            skLineSegment(sketch, "E49.4", {"start": v(-17.6, 15.41) * mm, "end": v(-13.6, 13.1) * mm});
            skLineSegment(sketch, "E49.5", {"start": v(-13.6, 13.1) * mm, "end": v(-13.6, 8.49) * mm});
            skPoint(sketch, "E49.0.midPoint", {"position": v(-15.6, 7.33) * mm});
            skPoint(sketch, "E50.0", {"position": v(-32.85, 10.8) * mm});
            skPoint(sketch, "E50.1", {"position": v(32.85, 10.8) * mm});
            skCircle(sketch, "E51.cCircle", {"center": v(17.6, 10.8) * mm, "radius": 3.9 * mm, "construction": true});
            skLineSegment(sketch, "E51.0", {"start": v(21.52, 8.54) * mm, "end": v(17.6, 6.29) * mm});
            skLineSegment(sketch, "E51.1", {"start": v(17.6, 6.29) * mm, "end": v(13.7, 8.54) * mm});
            skLineSegment(sketch, "E51.2", {"start": v(13.7, 8.54) * mm, "end": v(13.7, 13.05) * mm});
            skLineSegment(sketch, "E51.3", {"start": v(13.7, 13.05) * mm, "end": v(17.6, 15.3) * mm});
            skLineSegment(sketch, "E51.4", {"start": v(17.6, 15.3) * mm, "end": v(21.52, 13.05) * mm});
            skLineSegment(sketch, "E51.5", {"start": v(21.52, 13.05) * mm, "end": v(21.52, 8.54) * mm});
            skPoint(sketch, "E51.0.midPoint", {"position": v(19.56, 7.41) * mm});
            skLineSegment(sketch, "E52.1", {"start": v(-32.85, 21.59) * mm, "end": v(-32.85, 0) * mm});
            skLineSegment(sketch, "E52.2", {"start": v(32.85, 21.59) * mm, "end": v(32.85, 0) * mm});
            skCircle(sketch, "E53", {"center": v(-17.6, 10.8) * mm, "radius": 2 * mm});
            skCircle(sketch, "E54", {"center": v(17.6, 10.8) * mm, "radius": 2 * mm});
            skSolve(sketch);
        }
        {
            var Q0;
            Q0=makeQuery(id+"F22.imprint","IMPRINT",FACE,{"disambiguationData":[TD([[makeQuery(id+"F22.imprint","IMPRINT",EDGE,{"derivedFrom":sQuery(id+"F22.wireOp",EDGE,"E49.0")}),-1.0]])]});
            var Q1;
            Q1=makeQuery(id+"F22.imprint","IMPRINT",FACE,{"disambiguationData":[TD([[makeQuery(id+"F22.imprint","IMPRINT",EDGE,{"derivedFrom":sQuery(id+"F22.wireOp",EDGE,"E51.0")}),-1.0]])]});
            extrude(context, id + "F23", {"entities" : qUnion([Q0, Q1]), "operationType" : NewBodyOperationType.REMOVE, "oppositeDirection" : true, "depth" : 4 * mm, "offsetDistance" : 25.4 * mm});
        }
        {
            var Q0;
            Q0=makeQuery(id+"F22.imprint","IMPRINT",FACE,{"disambiguationData":[TD([[makeQuery(id+"F22.imprint","IMPRINT",EDGE,{"derivedFrom":sQuery(id+"F22.wireOp",EDGE,"E53")}),1.0]])]});
            var Q1;
            Q1=makeQuery(id+"F22.imprint","IMPRINT",FACE,{"disambiguationData":[TD([[makeQuery(id+"F22.imprint","IMPRINT",EDGE,{"derivedFrom":sQuery(id+"F22.wireOp",EDGE,"E54")}),1.0]])]});
            extrude(context, id + "F24", {"entities" : qUnion([Q0, Q1]), "operationType" : NewBodyOperationType.REMOVE, "oppositeDirection" : true, "depth" : 25.4 * mm, "offsetDistance" : 25.4 * mm});
        }
        {
            var Q0;
            Q0=qCreatedBy(makeId("Top.planeOp"),FACE);
            var sketch = newSketch(context, id + "F25", { "sketchPlane" : qUnion([Q0])});
            skPoint(sketch, "E55.0", {"position": v(-32.85, -133.92) * mm});
            skPoint(sketch, "E55.1", {"position": v(32.85, -133.92) * mm});
            skLineSegment(sketch, "E56.bottom", {"start": v(29.85, -115.61) * mm, "end": v(-29.85, -115.61) * mm});
            skLineSegment(sketch, "E56.top", {"start": v(29.85, -108) * mm, "end": v(-29.85, -108) * mm});
            skLineSegment(sketch, "E56.left", {"start": v(29.85, -115.61) * mm, "end": v(29.85, -108) * mm});
            skLineSegment(sketch, "E56.right", {"start": v(-29.85, -115.61) * mm, "end": v(-29.85, -108) * mm});
            skPoint(sketch, "E56.middle", {"position": v(0, -111.8) * mm});
            skSolve(sketch);
        }
        {
            var Q0;
            Q0=qSketchRegion(id+"F25",true);
            extrude(context, id + "F26", {"entities" : qUnion([Q0]), "depth" : 25.4 * mm, "offsetDistance" : 25.4 * mm});
        }
        {
            var Q0;
            Q0=makeQuery(id+"F26.opExtrude","CAP_EDGE",EDGE,{"disambiguationData":[OSD([sQuery(id+"F25.wireOp",EDGE,"E56.bottom")])],"isStart":false});
            var Q1;
            Q1=makeQuery(id+"F26.opExtrude","CAP_EDGE",EDGE,{"disambiguationData":[OSD([sQuery(id+"F25.wireOp",EDGE,"E56.top")])],"isStart":false});
            fillet(context, id + "F27", {"entities" : qUnion([Q0, Q1]), "radius" : 3.8 * mm, "tangentPropagation" : true, "allowEdgeOverflow" : false});
        }
        {
            var Q0;
            Q0=makeQuery(id+"F26.opExtrude","SWEPT_FACE",FACE,{"disambiguationData":[OSD([sQuery(id+"F25.wireOp",EDGE,"E56.bottom")])]});
            var sketch = newSketch(context, id + "F28", { "sketchPlane" : qUnion([Q0])});
            skCircle(sketch, "E57.0", {"center": v(-17.6, 10.8) * mm, "radius": 2 * mm});
            skCircle(sketch, "E57.1", {"center": v(17.6, 10.8) * mm, "radius": 2 * mm});
            skSolve(sketch);
        }
        {
            var Q0;
            Q0=makeQuery(id+"F28.imprint","IMPRINT",FACE,{"disambiguationData":[TD([[makeQuery(id+"F28.imprint","IMPRINT",EDGE,{"derivedFrom":sQuery(id+"F28.wireOp",EDGE,"E57.0")}),1.0]])]});
            var Q1;
            Q1=makeQuery(id+"F28.imprint","IMPRINT",FACE,{"disambiguationData":[TD([[makeQuery(id+"F28.imprint","IMPRINT",EDGE,{"derivedFrom":sQuery(id+"F28.wireOp",EDGE,"E57.1")}),1.0]])]});
            extrude(context, id + "F29", {"entities" : qUnion([Q0, Q1]), "operationType" : NewBodyOperationType.REMOVE, "oppositeDirection" : true, "depth" : 25.4 * mm, "offsetDistance" : 25.4 * mm});
        }
        {
            var Q0;
            Q0=qCreatedBy(makeId("Top.planeOp"),FACE);
            var sketch = newSketch(context, id + "F30", { "sketchPlane" : qUnion([Q0])});
            skCircle(sketch, "E58", {"center": v(177.8, 0) * mm, "radius": 2.12 * mm});
            skCircle(sketch, "E59", {"center": v(177.8, 0) * mm, "radius": 5 * mm});
            skCircle(sketch, "E60", {"center": v(197.58, 0) * mm, "radius": 2.12 * mm});
            skCircle(sketch, "E61", {"center": v(197.58, 0) * mm, "radius": 5 * mm});
            skSolve(sketch);
        }
        {
            var Q0;
            Q0=makeQuery(id+"F30.imprint","IMPRINT",FACE,{"disambiguationData":[TD([[makeQuery(id+"F30.imprint","IMPRINT",EDGE,{"derivedFrom":sQuery(id+"F30.wireOp",EDGE,"E58")}),-1.0]])]});
            extrude(context, id + "F31", {"entities" : qUnion([Q0]), "depth" : 2 * mm, "offsetDistance" : 25.4 * mm});
        }
        {
            var Q0;
            Q0=makeQuery(id+"F30.imprint","IMPRINT",FACE,{"disambiguationData":[TD([[makeQuery(id+"F30.imprint","IMPRINT",EDGE,{"derivedFrom":sQuery(id+"F30.wireOp",EDGE,"E60")}),-1.0]])]});
            extrude(context, id + "F32", {"entities" : qUnion([Q0]), "depth" : 5 * mm, "offsetDistance" : 25.4 * mm});
        }
    });
